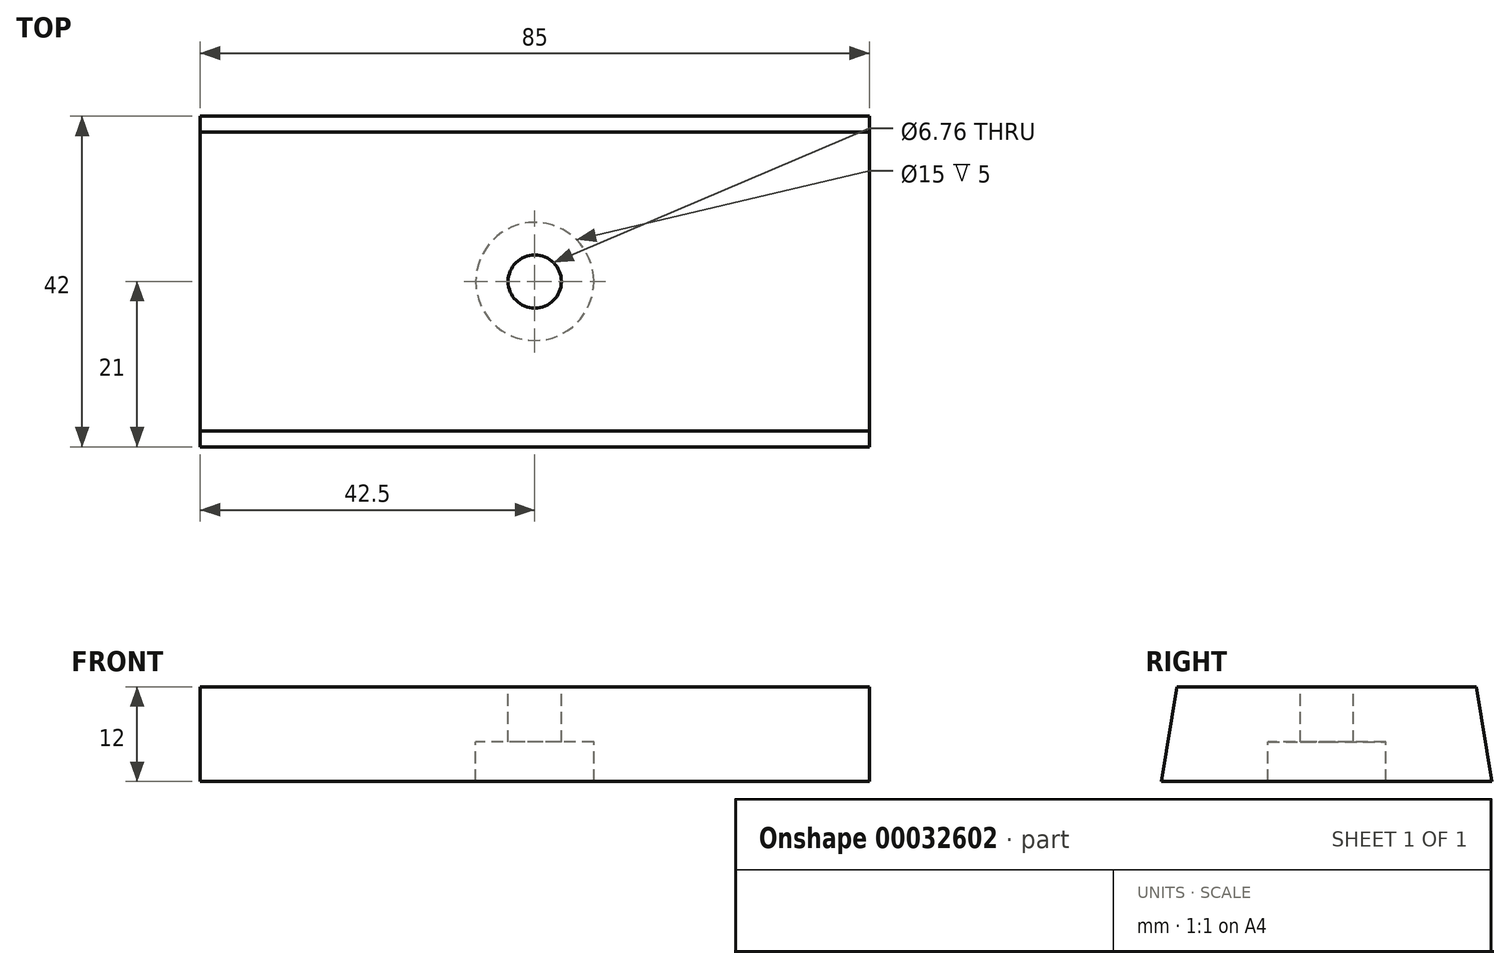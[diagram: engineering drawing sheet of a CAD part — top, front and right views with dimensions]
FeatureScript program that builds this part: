
annotation { "Feature Type Name" : "Feature", "Feature Type Description" : "" }
export const myFeature = defineFeature(function(context is Context, id is Id, definition is map)
    precondition{}
    {
        {
            var Q0;
            Q0=qCreatedBy(makeId("Right.planeOp"),FACE);
            var sketch = newSketch(context, id + "F0", { "sketchPlane" : qUnion([Q0])});
            skLineSegment(sketch, "E0.bottom", {"start": v(-19, 6) * mm, "end": v(19, 6) * mm});
            skLineSegment(sketch, "E0.top", {"start": v(-19, -6) * mm, "end": v(19, -6) * mm});
            skLineSegment(sketch, "E0.left", {"start": v(-19, 6) * mm, "end": v(-19, -6) * mm});
            skLineSegment(sketch, "E0.right", {"start": v(19, 6) * mm, "end": v(19, -6) * mm});
            skPoint(sketch, "E0.middle", {"position": v(0, 0) * mm});
            skLineSegment(sketch, "E1", {"start": v(19, -6) * mm, "end": v(21, -6) * mm});
            skLineSegment(sketch, "E2", {"start": v(21, -6) * mm, "end": v(19, 6) * mm});
            skLineSegment(sketch, "E3", {"start": v(-19, 6) * mm, "end": v(-21, -6) * mm});
            skLineSegment(sketch, "E4", {"start": v(-21, -6) * mm, "end": v(-19, -6) * mm});
            skSolve(sketch);
        }
        {
            var Q0;
            Q0=makeQuery(id+"F0.imprint","IMPRINT",FACE,{"disambiguationData":[TD([[makeQuery(id+"F0.imprint","IMPRINT",EDGE,{"derivedFrom":sQuery(id+"F0.wireOp",EDGE,"E0.bottom")}),-1.0]])]});
            var Q1;
            Q1=makeQuery(id+"F0.imprint","IMPRINT",FACE,{"disambiguationData":[TD([[makeQuery(id+"F0.imprint","IMPRINT",EDGE,{"derivedFrom":sQuery(id+"F0.wireOp",EDGE,"E0.right")}),1.0]])]});
            var Q2;
            Q2=makeQuery(id+"F0.imprint","IMPRINT",FACE,{"disambiguationData":[TD([[makeQuery(id+"F0.imprint","IMPRINT",EDGE,{"derivedFrom":sQuery(id+"F0.wireOp",EDGE,"E0.left")}),-1.0]])]});
            extrude(context, id + "F1", {"entities" : qUnion([Q0, Q1, Q2]), "depth" : 85 * mm});
        }
        {
            var Q0;
            Q0=makeQuery(id+"F1.opExtrude","SWEPT_FACE",FACE,{"disambiguationData":[OSD([sQuery(id+"F0.wireOp",EDGE,"E0.top"),sQuery(id+"F0.wireOp",EDGE,"E1"),sQuery(id+"F0.wireOp",EDGE,"E4")])]});
            var sketch = newSketch(context, id + "F2", { "sketchPlane" : qUnion([Q0])});
            skLineSegment(sketch, "E5", {"start": v(0, 0) * mm, "end": v(85, 0) * mm, "construction": true});
            skLineSegment(sketch, "E6", {"start": v(42.5, 21) * mm, "end": v(42.5, -21) * mm, "construction": true});
            skPoint(sketch, "E7", {"position": v(42.5, 0) * mm});
            skSolve(sketch);
        }
        {
            var Q0;
            Q0=sQuery(id+"F2.wireOp",VERTEX,"E7");
            var Q1;
            Q1=makeQuery(id+"F1.opExtrude","SWEPT_BODY",BODY,{"disambiguationData":[OSD([sQuery(id+"F0.wireOp",EDGE,"E0.bottom"),sQuery(id+"F0.wireOp",EDGE,"E0.top"),sQuery(id+"F0.wireOp",EDGE,"E1"),sQuery(id+"F0.wireOp",EDGE,"E2"),sQuery(id+"F0.wireOp",EDGE,"E3"),sQuery(id+"F0.wireOp",EDGE,"E4")])]});
            hole(context, id + "F3", {"style" : HoleStyle.C_BORE, "endStyle" : HoleEndStyle.THROUGH, "holeDiameter" : 6.76 * mm, "cBoreDiameter" : 15 * mm, "cBoreDepth" : 5 * mm, "locations" : qUnion([Q0]), "scope" : qUnion([Q1]), "isTappedThrough" : true});
        }
    });
